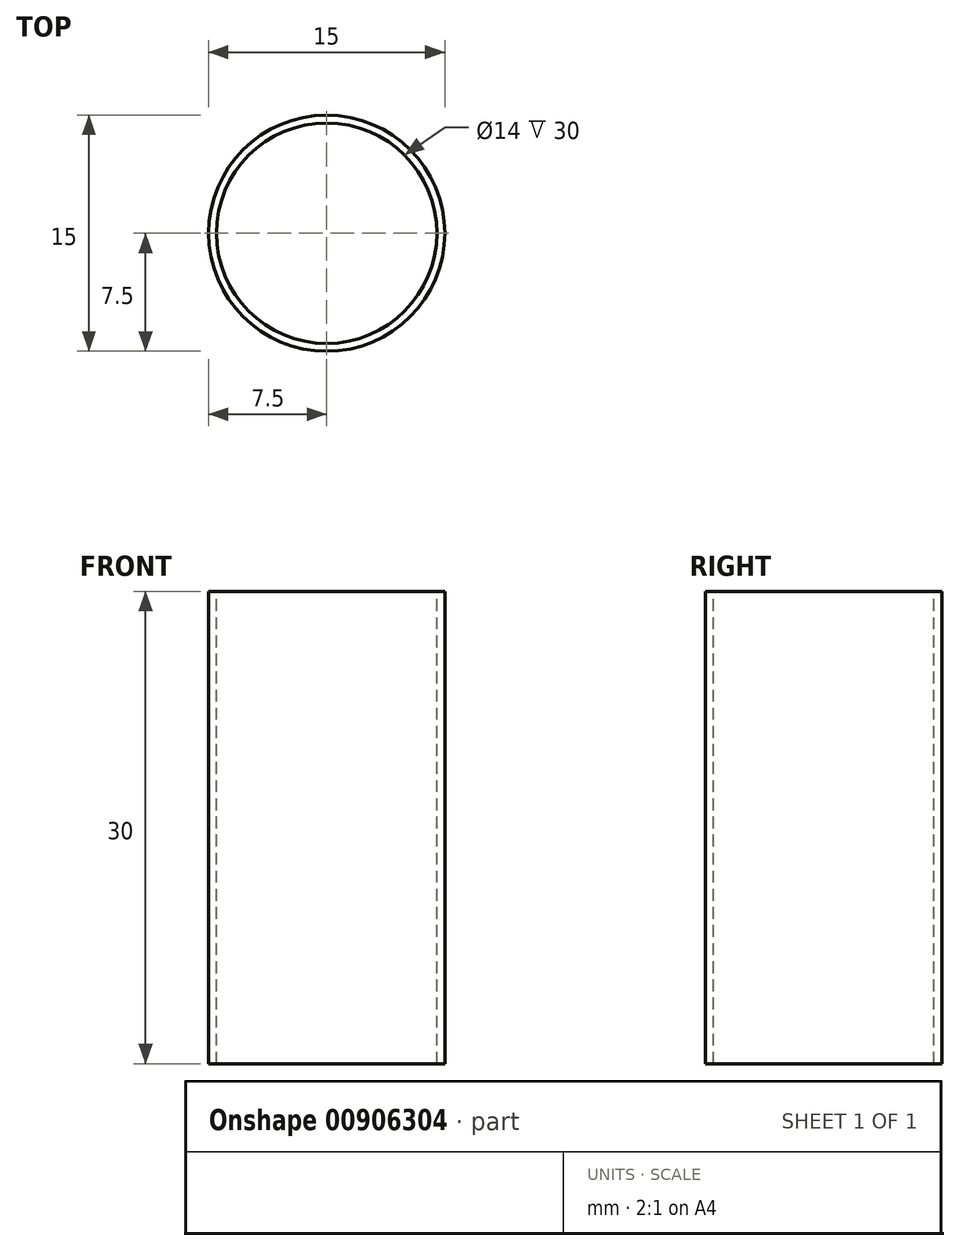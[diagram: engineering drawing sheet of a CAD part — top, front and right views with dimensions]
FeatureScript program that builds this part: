
annotation { "Feature Type Name" : "Feature", "Feature Type Description" : "" }
export const myFeature = defineFeature(function(context is Context, id is Id, definition is map)
    precondition{}
    {
        {
            var Q0;
            Q0=qCreatedBy(makeId("Top.planeOp"),FACE);
            var sketch = newSketch(context, id + "F0", { "sketchPlane" : qUnion([Q0])});
            skCircle(sketch, "E0", {"center": v(0, 0) * mm, "radius": 7.5 * mm});
            skCircle(sketch, "E1", {"center": v(0, 0) * mm, "radius": 7 * mm});
            skSolve(sketch);
        }
        {
            var Q0;
            Q0=qCreatedBy(makeId("Front.planeOp"),FACE);
            var sketch = newSketch(context, id + "F1", { "sketchPlane" : qUnion([Q0])});
            skLineSegment(sketch, "E2", {"start": v(0, 0) * mm, "end": v(0, 30) * mm});
            skSolve(sketch);
        }
        {
            var Q0;
            Q0=makeQuery(id+"F0.imprint","IMPRINT",FACE,{"disambiguationData":[TD([[makeQuery(id+"F0.imprint","IMPRINT",EDGE,{"derivedFrom":sQuery(id+"F0.wireOp",EDGE,"E0")}),1.0]])]});
            var Q1;
            Q1=sQuery(id+"F1.wireOp",EDGE,"E2");
            sweep(context, id + "F2", {"profiles" : qUnion([Q0]), "path" : qUnion([Q1])});
        }
    });
